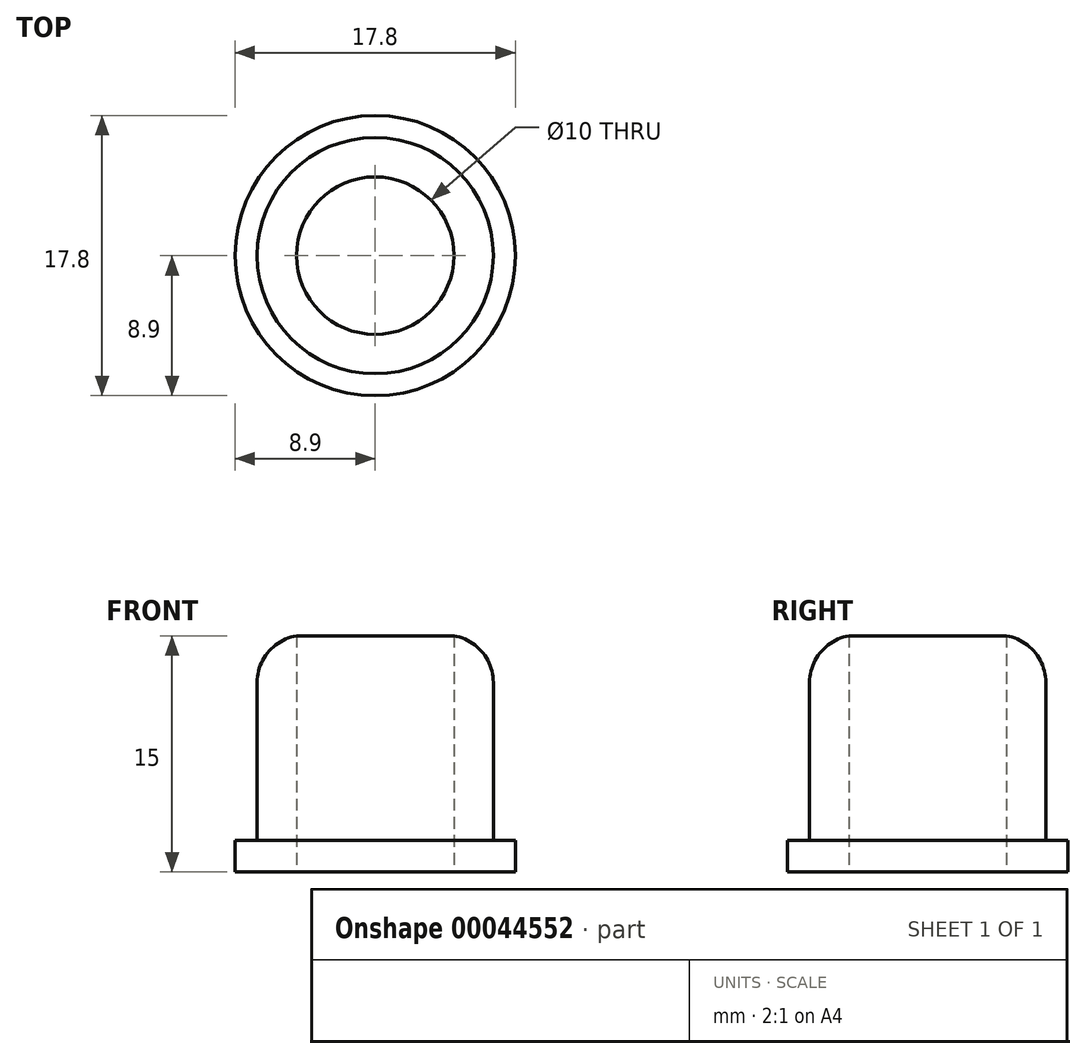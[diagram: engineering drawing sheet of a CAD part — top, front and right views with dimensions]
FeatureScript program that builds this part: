
annotation { "Feature Type Name" : "Feature", "Feature Type Description" : "" }
export const myFeature = defineFeature(function(context is Context, id is Id, definition is map)
    precondition{}
    {
        {
            var Q0;
            Q0=qCreatedBy(makeId("Top.planeOp"),FACE);
            var sketch = newSketch(context, id + "F0", { "sketchPlane" : qUnion([Q0])});
            skCircle(sketch, "E0", {"center": v(0, 0) * mm, "radius": 7.5 * mm});
            skSolve(sketch);
        }
        {
            var Q0;
            Q0=makeQuery(id+"F0.imprint","IMPRINT",FACE,{"disambiguationData":[TD([[makeQuery(id+"F0.imprint","IMPRINT",EDGE,{"derivedFrom":sQuery(id+"F0.wireOp",EDGE,"E0")}),1.0]])]});
            extrude(context, id + "F1", {"entities" : qUnion([Q0]), "depth" : 15 * mm});
        }
        {
            var Q0;
            Q0=qSketchRegion(id+"F0",true);
            var sketch = newSketch(context, id + "F2", { "sketchPlane" : qUnion([Q0])});
            skCircle(sketch, "E1", {"center": v(0, 0) * mm, "radius": 8.9 * mm});
            skSolve(sketch);
        }
        {
            var Q0;
            Q0=makeQuery(id+"F2.imprint","IMPRINT",FACE,{"disambiguationData":[TD([[makeQuery(id+"F2.imprint","IMPRINT",EDGE,{"derivedFrom":sQuery(id+"F2.wireOp",EDGE,"E1")}),1.0]])]});
            extrude(context, id + "F3", {"entities" : qUnion([Q0]), "operationType" : NewBodyOperationType.ADD, "depth" : 2 * mm});
        }
        {
            var Q0;
            Q0=makeQuery(id+"F1.opExtrude","CAP_FACE",FACE,{"disambiguationData":[OSD([sQuery(id+"F0.wireOp",EDGE,"E0")])],"isStart":false});
            var Q1;
            {var subQ0=sQuery(id+"F0.wireOp",EDGE,"E0");Q1=makeQuery(id+"F3.boolean.opBoolean","MERGE",FACE,{"derivedFrom":[makeQuery(id+"F1.opExtrude","CAP_FACE",FACE,{"disambiguationData":[OSD([subQ0])],"isStart":true}),makeQuery(id+"F3.opExtrude","CAP_FACE",FACE,{"disambiguationData":[OSD([subQ0,sQuery(id+"F2.wireOp",EDGE,"E1")])],"isStart":true})]});}
            shell(context, id + "F4", {"entities" : qUnion([Q0, Q1]), "thickness" : 2.5 * mm});
        }
        {
            var Q0;
            Q0=makeQuery(id+"F1.opExtrude","CAP_EDGE",EDGE,{"disambiguationData":[OSD([sQuery(id+"F0.wireOp",EDGE,"E0")])],"isStart":false});
            fillet(context, id + "F5", {"entities" : qUnion([Q0]), "radius" : 3 * mm, "tangentPropagation" : true, "allowEdgeOverflow" : false});
        }
    });
